# Revit family: GR_Адаптер линейный_Муфта(n)_PV-КСД_R21
name_source: partatom
category: Соединительные детали воздуховодов
units: mm (PartAtom-declared; Revit-internal decimal feet)

## family parameters
Всегда вертикально = Да
Заголовок OmniClass = Metal Ducts
На основе рабочей плоскости = Нет
Номер OmniClass = 23.75.70.14.31
Общий = Нет
При загрузке вырезать с полостями = Нет
Размер круглого соединителя = Использовать диаметр
Тип детали = Мультипорт

## types (15) — shared parameters
ADSK_URL страницы изделия = https://grilles.ru
ADSK_Версия Revit = 2021
ADSK_Единица измерения = шт.
ADSK_Завод-изготовитель = ООО "ВЕНТРЕШЕТКИКОМ"
ADSK_Код изделия = 002092
ADSK_Количество = 1
ADSK_Материал = ADSK_Оцинкованная сталь
ADSK_Наименование = PV-КСД, адаптер вентиляционной решётки радиальный
Изготовитель = ООО "ВЕНТРЕШЕТКИКОМ"
Корпус_Металл_Толщина = 1 мм
Муфта_Металл_Толщина = 1 мм
zero-valued in all types: Отметка по умолчанию

## per-type parameters (varying)
| type | Корпус_Высота | Корпус_Длина | Решётка_Высота | Решётка_Положение_Центр |
| PV-КСД 1-20 | 182 мм | 90 мм | 48 мм | 45 мм |
| PV-КСД 1-30 | 182 мм | 95 мм | 58 мм | 48 мм |
| PV-КСД 1-40 | 222 мм | 100 мм | 68 мм | 50 мм |
| PV-КСД 1-50 | 222 мм | 105 мм | 78 мм | 53 мм |
| PV-КСД 1-60 | 272 мм | 110 мм | 88 мм | 55 мм |
| PV-КСД 1-70 | 272 мм | 115 мм | 98 мм | 58 мм |
| PV-КСД 2-20 | 222 мм | 135 мм | 95 мм | 68 мм |
| PV-КСД 2-25 | 222 мм | 145 мм | 105 мм | 73 мм |
| PV-КСД 2-30 | 222 мм | 155 мм | 115 мм | 78 мм |
| PV-КСД 3-20 | 222 мм | 185 мм | 142 мм | 93 мм |
| PV-КСД 3-25 | 222 мм | 200 мм | 157 мм | 100 мм |
| PV-КСД 3-30 | 222 мм | 215 мм | 172 мм | 108 мм |
| PV-КСД 4-20 | 272 мм | 230 мм | 189 мм | 115 мм |
| PV-КСД 4-25 | 272 мм | 250 мм | 209 мм | 125 мм |
| PV-КСД 4-30 | 272 мм | 270 мм | 229 мм | 135 мм |

note: column(s) folded — value = type name in every type: ADSK_Марка
